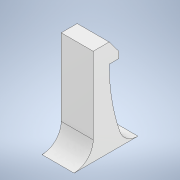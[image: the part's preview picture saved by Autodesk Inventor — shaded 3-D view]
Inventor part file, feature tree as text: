
AUTODESK INVENTOR PART (.ipt)
format: ipt  version: 2022 (Build 260153000, 153)  size: 153,600 bytes
history: native  units: mm
features: extrude x1, sketch x1
ambient origin geometry x8: Origin, YZ Plane, XZ Plane, XY Plane, X Axis, Y Axis, Z Axis, Center Point
bodies: Solid1 (feature_tree)
feature tree (2):
  extrude  "Extrusion1"  Depth=4.0mm
  sketch  "Sketch1"  dims[d0=12.0mm d1=4.0mm d2=1.5mm d3=3.0mm d4=2.5mm d5=1.0mm d6=5.0mm d7=0.0mm d15=3.0mm d17=3.0mm d18=3.0mm]
